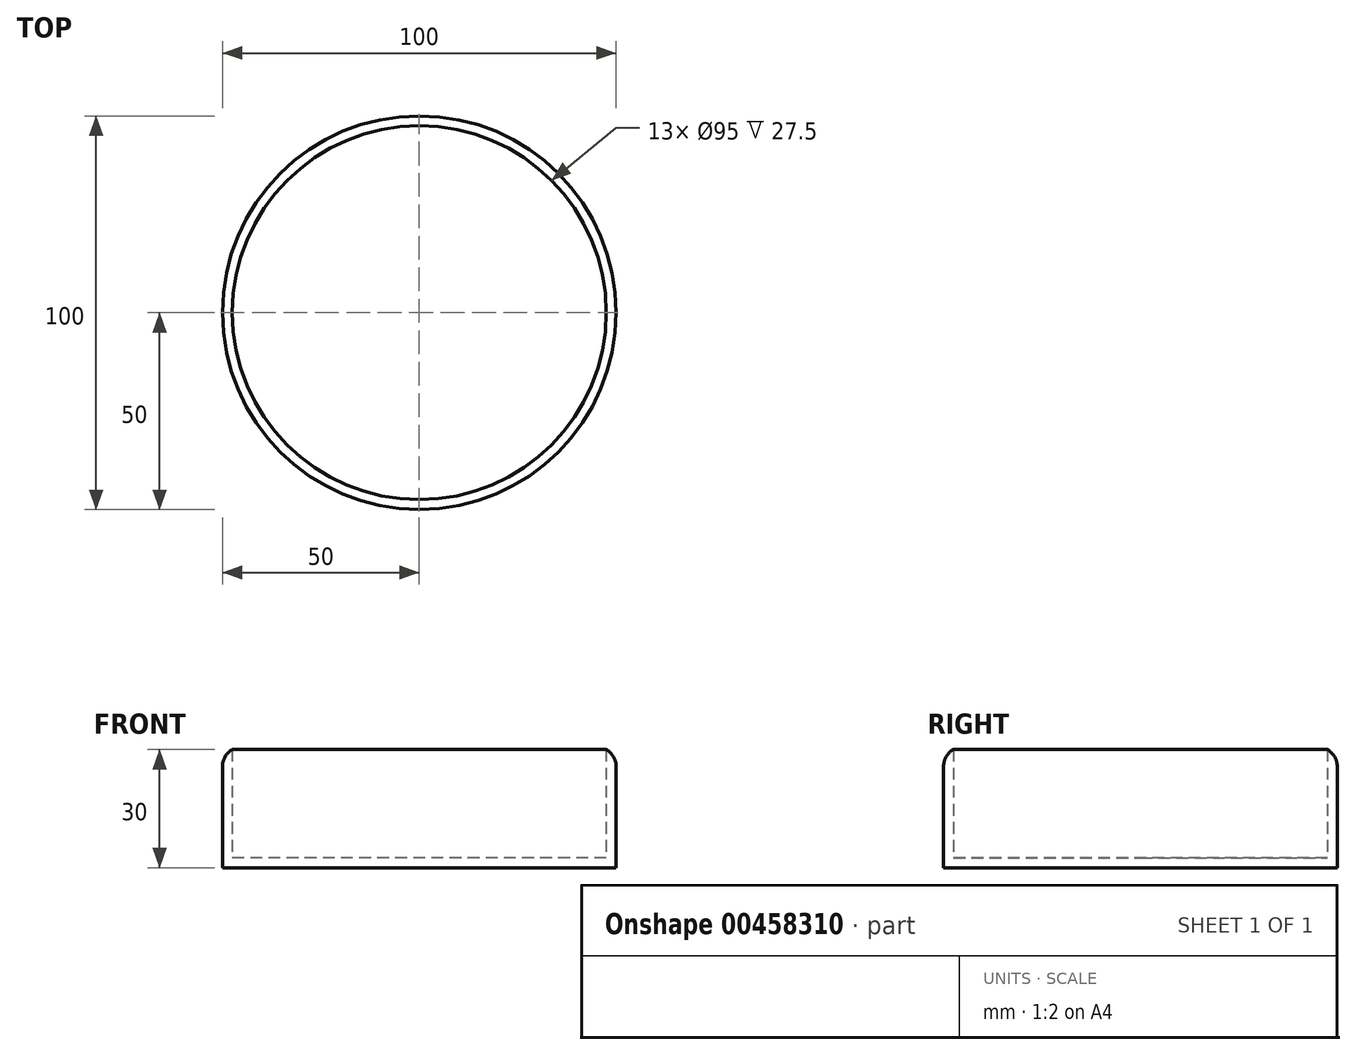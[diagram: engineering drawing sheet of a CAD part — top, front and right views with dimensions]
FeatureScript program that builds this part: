
annotation { "Feature Type Name" : "Feature", "Feature Type Description" : "" }
export const myFeature = defineFeature(function(context is Context, id is Id, definition is map)
    precondition{}
    {
        {
            var Q0;
            Q0=qCreatedBy(makeId("Top.planeOp"),FACE);
            var sketch = newSketch(context, id + "F0", { "sketchPlane" : qUnion([Q0])});
            skCircle(sketch, "E0", {"center": v(0, 0) * mm, "radius": 50 * mm});
            skSolve(sketch);
        }
        {
            var Q0;
            Q0=makeQuery(id+"F0.imprint","IMPRINT",FACE,{"disambiguationData":[TD([[makeQuery(id+"F0.imprint","IMPRINT",EDGE,{"derivedFrom":sQuery(id+"F0.wireOp",EDGE,"E0")}),1.0]])]});
            extrude(context, id + "F1", {"entities" : qUnion([Q0]), "depth" : 30 * mm});
        }
        {
            var Q0;
            Q0=makeQuery(id+"F1.opExtrude","CAP_FACE",FACE,{"disambiguationData":[OSD([sQuery(id+"F0.wireOp",EDGE,"E0")])],"isStart":false});
            shell(context, id + "F2", {"entities" : qUnion([Q0]), "thickness" : 2.5 * mm});
        }
        {
            var Q0;
            Q0=makeQuery(id+"F1.opExtrude","CAP_EDGE",EDGE,{"disambiguationData":[OSD([sQuery(id+"F0.wireOp",EDGE,"E0")])],"isStart":false});
            fillet(context, id + "F3", {"entities" : qUnion([Q0]), "radius" : 5 * mm, "tangentPropagation" : true, "allowEdgeOverflow" : false});
        }
    });
